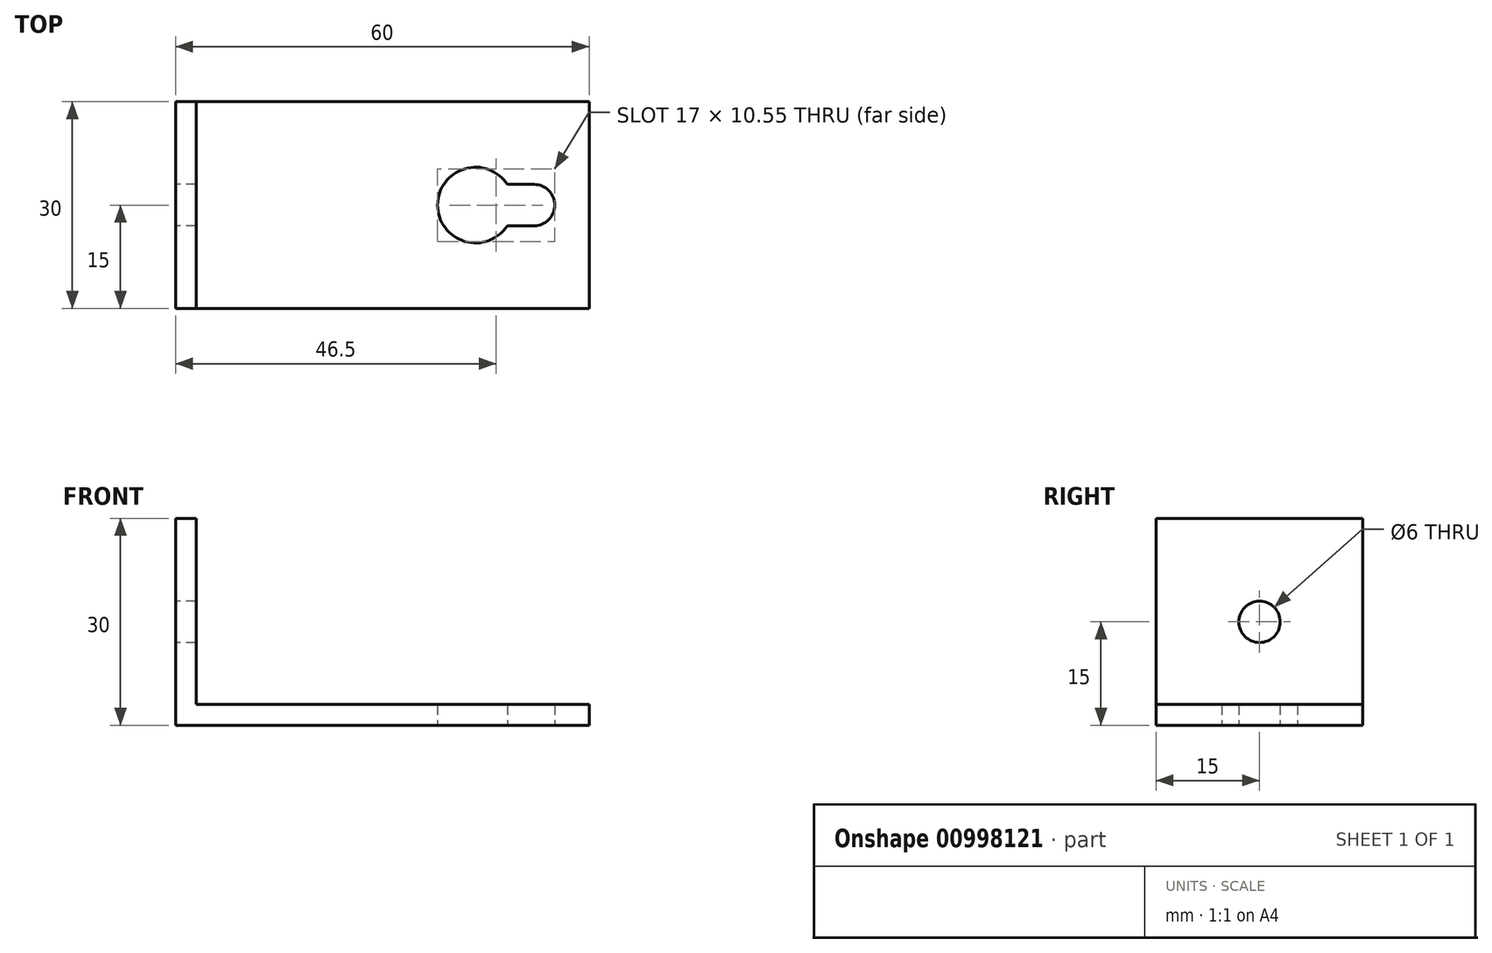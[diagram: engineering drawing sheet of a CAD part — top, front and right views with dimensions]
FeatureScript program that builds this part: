
annotation { "Feature Type Name" : "Feature", "Feature Type Description" : "" }
export const myFeature = defineFeature(function(context is Context, id is Id, definition is map)
    precondition{}
    {
        {
            var Q0;
            Q0=qCreatedBy(makeId("Front.planeOp"),FACE);
            var sketch = newSketch(context, id + "F0", { "sketchPlane" : qUnion([Q0])});
            skLineSegment(sketch, "E0", {"start": v(0, 0) * mm, "end": v(0, 30) * mm});
            skLineSegment(sketch, "E1", {"start": v(0, 30) * mm, "end": v(3, 30) * mm});
            skLineSegment(sketch, "E2", {"start": v(3, 30) * mm, "end": v(3, 3) * mm});
            skLineSegment(sketch, "E3", {"start": v(3, 3) * mm, "end": v(60, 3) * mm});
            skLineSegment(sketch, "E4", {"start": v(60, 3) * mm, "end": v(60, 0) * mm});
            skLineSegment(sketch, "E5", {"start": v(60, 0) * mm, "end": v(0, 0) * mm});
            skSolve(sketch);
        }
        {
            var Q0;
            Q0 = qSketchRegion(id + "F0", true);
            extrude(context, id + "F1", {"entities" : qUnion([Q0]), "depth" : 30 * mm, "offsetDistance" : 25 * mm});
        }
        {
            var Q0;
            Q0=makeQuery(id+"F1.opExtrude","SWEPT_FACE",FACE,{"disambiguationData":[OSD([sQuery(id+"F0.wireOp",EDGE,"E0")])]});
            var sketch = newSketch(context, id + "F2", { "sketchPlane" : qUnion([Q0])});
            skLineSegment(sketch, "E6", {"start": v(15, 30) * mm, "end": v(15, 0) * mm, "construction": true});
            skLineSegment(sketch, "E7", {"start": v(0, 15) * mm, "end": v(30, 15) * mm, "construction": true});
            skCircle(sketch, "E8", {"center": v(15, 15) * mm, "radius": 3 * mm});
            skSolve(sketch);
        }
        {
            var Q0;
            Q0=makeQuery(id+"F2.imprint","IMPRINT",FACE,{"disambiguationData":[TD([[makeQuery(id+"F2.imprint","IMPRINT",EDGE,{"derivedFrom":sQuery(id+"F2.wireOp",EDGE,"E8")}),1.0]])]});
            var Q1;
            Q1=sQuery(id+"F2.wireOp",EDGE,"E8");
            extrude(context, id + "F3", {"entities" : qUnion([Q0]), "operationType" : NewBodyOperationType.REMOVE, "surfaceEntities" : qUnion([Q1]), "endBound" : BoundingType.THROUGH_ALL, "oppositeDirection" : true, "depth" : 25 * mm, "offsetDistance" : 25 * mm});
        }
        {
            var Q0;
            Q0=makeQuery(id+"F1.opExtrude","SWEPT_FACE",FACE,{"disambiguationData":[OSD([sQuery(id+"F0.wireOp",EDGE,"E5")])]});
            var sketch = newSketch(context, id + "F4", { "sketchPlane" : qUnion([Q0])});
            skLineSegment(sketch, "E9", {"start": v(60, 15) * mm, "end": v(0, 15) * mm, "construction": true});
            skArc(sketch, "E10", {"start": v(48.1, 18) * mm, "mid": v(38, 15) * mm, "end": v(48.1, 12) * mm});
            skArc(sketch, "E11", {"start": v(52, 12) * mm, "mid": v(55, 15) * mm, "end": v(52, 18) * mm});
            skLineSegment(sketch, "E12", {"start": v(52, 18) * mm, "end": v(48.1, 18) * mm});
            skLineSegment(sketch, "E13", {"start": v(52, 12) * mm, "end": v(48.1, 12) * mm});
            skLineSegment(sketch, "E14", {"start": v(52, 30) * mm, "end": v(52, 0) * mm, "construction": true});
            skCircle(sketch, "E15", {"center": v(43.5, 15) * mm, "radius": 5.5 * mm, "construction": true});
            skCircle(sketch, "E16", {"center": v(52, 15) * mm, "radius": 3 * mm, "construction": true});
            skSolve(sketch);
        }
        {
            var Q0;
            Q0=makeQuery(id+"F4.imprint","IMPRINT",FACE,{"disambiguationData":[TD([[makeQuery(id+"F4.imprint","IMPRINT",EDGE,{"derivedFrom":sQuery(id+"F4.wireOp",EDGE,"E10")}),1.0]])]});
            extrude(context, id + "F5", {"entities" : qUnion([Q0]), "operationType" : NewBodyOperationType.REMOVE, "endBound" : BoundingType.THROUGH_ALL, "oppositeDirection" : true, "depth" : 25 * mm, "offsetDistance" : 25 * mm});
        }
    });
